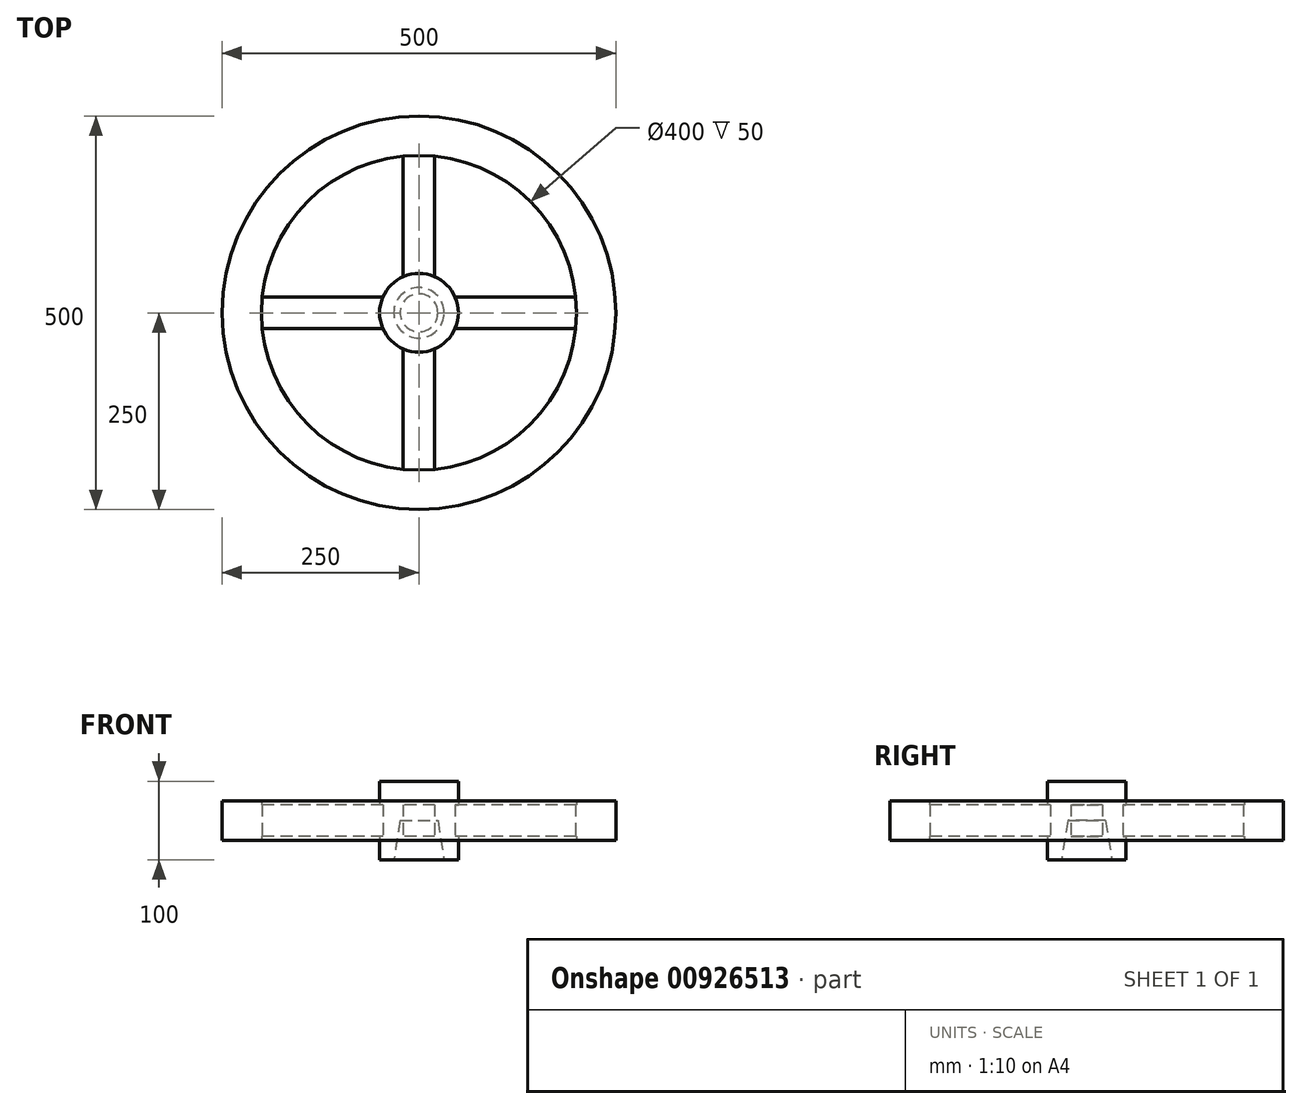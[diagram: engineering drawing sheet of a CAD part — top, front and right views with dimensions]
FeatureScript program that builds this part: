
annotation { "Feature Type Name" : "Feature", "Feature Type Description" : "" }
export const myFeature = defineFeature(function(context is Context, id is Id, definition is map)
    precondition{}
    {
        {
            var Q0;
            Q0=qCreatedBy(makeId("Top.planeOp"),FACE);
            var sketch = newSketch(context, id + "F0", { "sketchPlane" : qUnion([Q0])});
            skCircle(sketch, "E0", {"center": v(0, 0) * mm, "radius": 50 * mm});
            skCircle(sketch, "E1", {"center": v(0, 0) * mm, "radius": 200 * mm});
            skCircle(sketch, "E2", {"center": v(0, 0) * mm, "radius": 250 * mm});
            skLineSegment(sketch, "E3.bottom", {"start": v(220.8, -20) * mm, "end": v(-220.8, -20) * mm});
            skLineSegment(sketch, "E3.top", {"start": v(220.8, 20) * mm, "end": v(-220.8, 20) * mm});
            skLineSegment(sketch, "E3.left", {"start": v(220.8, -20) * mm, "end": v(220.8, 20) * mm});
            skLineSegment(sketch, "E3.right", {"start": v(-220.8, -20) * mm, "end": v(-220.8, 20) * mm});
            skLineSegment(sketch, "E4.bottom", {"start": v(-20, 220.8) * mm, "end": v(20, 220.8) * mm});
            skLineSegment(sketch, "E4.top", {"start": v(-20, -220.8) * mm, "end": v(20, -220.8) * mm});
            skLineSegment(sketch, "E4.left", {"start": v(-20, 220.8) * mm, "end": v(-20, -220.8) * mm});
            skLineSegment(sketch, "E4.right", {"start": v(20, 220.8) * mm, "end": v(20, -220.8) * mm});
            skSolve(sketch);
        }
        {
            var Q0;
            Q0=makeQuery(id+"F0.imprint","IMPRINT",FACE,{"disambiguationData":[TD([[makeQuery(id+"F0.imprint","IMPRINT",EDGE,{"derivedFrom":sQuery(id+"F0.wireOp",EDGE,"E1")}),-1.0]])]});
            var Q1;
            {var subQ5=sQuery(id+"F0.wireOp",EDGE,"E3.right");Q1=makeQuery(id+"F0.imprint","IMPRINT",FACE,{"disambiguationData":[TD([[makeQuery(id+"F0.imprint","IMPRINT",EDGE,{"derivedFrom":subQ5}),-1.0]])]});}
            var Q2;
            {var subQ5=sQuery(id+"F0.wireOp",EDGE,"E4.top");Q2=makeQuery(id+"F0.imprint","IMPRINT",FACE,{"disambiguationData":[TD([[makeQuery(id+"F0.imprint","IMPRINT",EDGE,{"derivedFrom":subQ5}),1.0]])]});}
            var Q3;
            {var subQ5=sQuery(id+"F0.wireOp",EDGE,"E3.left");Q3=makeQuery(id+"F0.imprint","IMPRINT",FACE,{"disambiguationData":[TD([[makeQuery(id+"F0.imprint","IMPRINT",EDGE,{"derivedFrom":subQ5}),1.0]])]});}
            var Q4;
            {var subQ5=sQuery(id+"F0.wireOp",EDGE,"E4.bottom");Q4=makeQuery(id+"F0.imprint","IMPRINT",FACE,{"disambiguationData":[TD([[makeQuery(id+"F0.imprint","IMPRINT",EDGE,{"derivedFrom":subQ5}),-1.0]])]});}
            extrude(context, id + "F1", {"entities" : qUnion([Q0, Q1, Q2, Q3, Q4]), "endBound" : BoundingType.SYMMETRIC, "depth" : 50 * mm, "offsetDistance" : 25 * mm});
        }
        {
            var Q0;
            Q0=makeQuery(id+"F0.imprint","IMPRINT",FACE,{"disambiguationData":[TD([[makeQuery(id+"F0.imprint","IMPRINT",EDGE,{"derivedFrom":sQuery(id+"F0.wireOp",EDGE,"E0")}),1.0]])]});
            var Q1;
            {var subQ0=sQuery(id+"F0.wireOp",EDGE,"E3.top");var subQ1=sQuery(id+"F0.wireOp",EDGE,"E0");var subQ2=makeQuery(id+"F0.imprint","INTERSECT",VERTEX,{"disambiguationData":[OD(1.0)],"derivedFrom":[subQ1,subQ0]});Q1=makeQuery(id+"F0.imprint","IMPRINT",FACE,{"disambiguationData":[TD([[makeQuery(id+"F0.imprint","IMPRINT",EDGE,{"disambiguationData":[TD([[subQ2,-1.0]])],"derivedFrom":subQ1}),1.0]])]});}
            var Q2;
            {var subQ0=sQuery(id+"F0.wireOp",EDGE,"E4.right");var subQ1=sQuery(id+"F0.wireOp",EDGE,"E3.bottom");var subQ2=makeQuery(id+"F0.imprint","INTERSECT",VERTEX,{"derivedFrom":[subQ1,subQ0]});Q2=makeQuery(id+"F0.imprint","IMPRINT",FACE,{"disambiguationData":[TD([[makeQuery(id+"F0.imprint","IMPRINT",EDGE,{"disambiguationData":[TD([[subQ2,-1.0]])],"derivedFrom":subQ1}),-1.0]])]});}
            var Q3;
            {var subQ0=sQuery(id+"F0.wireOp",EDGE,"E4.left");var subQ1=sQuery(id+"F0.wireOp",EDGE,"E0");var subQ2=makeQuery(id+"F0.imprint","INTERSECT",VERTEX,{"disambiguationData":[OD(1.0)],"derivedFrom":[subQ1,subQ0]});Q3=makeQuery(id+"F0.imprint","IMPRINT",FACE,{"disambiguationData":[TD([[makeQuery(id+"F0.imprint","IMPRINT",EDGE,{"disambiguationData":[TD([[subQ2,-1.0]])],"derivedFrom":subQ1}),1.0]])]});}
            var Q4;
            {var subQ0=sQuery(id+"F0.wireOp",EDGE,"E3.top");var subQ1=sQuery(id+"F0.wireOp",EDGE,"E0");var subQ2=makeQuery(id+"F0.imprint","INTERSECT",VERTEX,{"disambiguationData":[OD(0.0)],"derivedFrom":[subQ1,subQ0]});Q4=makeQuery(id+"F0.imprint","IMPRINT",FACE,{"disambiguationData":[TD([[makeQuery(id+"F0.imprint","IMPRINT",EDGE,{"disambiguationData":[TD([[subQ2,1.0]])],"derivedFrom":subQ1}),1.0]])]});}
            var Q5;
            {var subQ0=sQuery(id+"F0.wireOp",EDGE,"E4.right");var subQ1=sQuery(id+"F0.wireOp",EDGE,"E0");var subQ2=makeQuery(id+"F0.imprint","INTERSECT",VERTEX,{"disambiguationData":[OD(0.0)],"derivedFrom":[subQ1,subQ0]});Q5=makeQuery(id+"F0.imprint","IMPRINT",FACE,{"disambiguationData":[TD([[makeQuery(id+"F0.imprint","IMPRINT",EDGE,{"disambiguationData":[TD([[subQ2,-1.0]])],"derivedFrom":subQ1}),1.0]])]});}
            extrude(context, id + "F2", {"entities" : qUnion([Q0, Q1, Q2, Q3, Q4, Q5]), "endBound" : BoundingType.SYMMETRIC, "depth" : 100 * mm, "offsetDistance" : 25 * mm});
        }
        {
            var Q0;
            {var subQ0=sQuery(id+"F0.wireOp",EDGE,"E3.top");var subQ1=sQuery(id+"F0.wireOp",EDGE,"E0");var subQ2=makeQuery(id+"F0.imprint","INTERSECT",VERTEX,{"disambiguationData":[OD(1.0)],"derivedFrom":[subQ1,subQ0]});Q0=makeQuery(id+"F0.imprint","IMPRINT",FACE,{"disambiguationData":[TD([[makeQuery(id+"F0.imprint","IMPRINT",EDGE,{"disambiguationData":[TD([[subQ2,-1.0]])],"derivedFrom":subQ1}),-1.0]])]});}
            var Q1;
            {var subQ0=sQuery(id+"F0.wireOp",EDGE,"E4.right");var subQ1=sQuery(id+"F0.wireOp",EDGE,"E0");var subQ2=makeQuery(id+"F0.imprint","INTERSECT",VERTEX,{"disambiguationData":[OD(0.0)],"derivedFrom":[subQ1,subQ0]});Q1=makeQuery(id+"F0.imprint","IMPRINT",FACE,{"disambiguationData":[TD([[makeQuery(id+"F0.imprint","IMPRINT",EDGE,{"disambiguationData":[TD([[subQ2,-1.0]])],"derivedFrom":subQ1}),-1.0]])]});}
            var Q2;
            {var subQ0=sQuery(id+"F0.wireOp",EDGE,"E3.top");var subQ1=sQuery(id+"F0.wireOp",EDGE,"E0");var subQ2=makeQuery(id+"F0.imprint","INTERSECT",VERTEX,{"disambiguationData":[OD(0.0)],"derivedFrom":[subQ1,subQ0]});Q2=makeQuery(id+"F0.imprint","IMPRINT",FACE,{"disambiguationData":[TD([[makeQuery(id+"F0.imprint","IMPRINT",EDGE,{"disambiguationData":[TD([[subQ2,1.0]])],"derivedFrom":subQ1}),-1.0]])]});}
            var Q3;
            {var subQ0=sQuery(id+"F0.wireOp",EDGE,"E4.left");var subQ1=sQuery(id+"F0.wireOp",EDGE,"E0");var subQ2=makeQuery(id+"F0.imprint","INTERSECT",VERTEX,{"disambiguationData":[OD(1.0)],"derivedFrom":[subQ1,subQ0]});Q3=makeQuery(id+"F0.imprint","IMPRINT",FACE,{"disambiguationData":[TD([[makeQuery(id+"F0.imprint","IMPRINT",EDGE,{"disambiguationData":[TD([[subQ2,-1.0]])],"derivedFrom":subQ1}),-1.0]])]});}
            extrude(context, id + "F3", {"entities" : qUnion([Q0, Q1, Q2, Q3]), "operationType" : NewBodyOperationType.ADD, "endBound" : BoundingType.SYMMETRIC, "depth" : 40 * mm, "offsetDistance" : 25 * mm});
        }
        {
            var Q0;
            Q0=qCreatedBy(makeId("Front.planeOp"),FACE);
            var sketch = newSketch(context, id + "F4", { "sketchPlane" : qUnion([Q0])});
            skLineSegment(sketch, "E5", {"start": v(0, 0) * mm, "end": v(0, -50) * mm});
            skLineSegment(sketch, "E6.0.0", {"start": v(50, -50) * mm, "end": v(-50, -50) * mm});
            skLineSegment(sketch, "E7", {"start": v(-32, -50) * mm, "end": v(-24, 0) * mm});
            skLineSegment(sketch, "E8", {"start": v(-24, 0) * mm, "end": v(0, 0) * mm});
            skLineSegment(sketch, "E9.MirrorCS", {"start": v(24, 0) * mm, "end": v(0, 0) * mm, "construction": true});
            skLineSegment(sketch, "E10.MirrorCS", {"start": v(32, -50) * mm, "end": v(24, 0) * mm, "construction": true});
            skSolve(sketch);
        }
        {
            var Q0;
            {var subQ0=sQuery(id+"F4.wireOp",EDGE,"E5");Q0=makeQuery(id+"F4.imprint","IMPRINT",FACE,{"disambiguationData":[TD([[makeQuery(id+"F4.imprint","IMPRINT",EDGE,{"derivedFrom":subQ0}),-1.0]])]});}
            var Q1;
            Q1=sQuery(id+"F4.wireOp",EDGE,"E5");
            revolve(context, id + "F5", {"operationType" : NewBodyOperationType.REMOVE, "surfaceOperationType" : NewSurfaceOperationType.NEW, "entities" : qUnion([Q0]), "axis" : qUnion([Q1]), "revolveType" : RevolveType.FULL, "oppositeDirection" : true});
        }
    });
